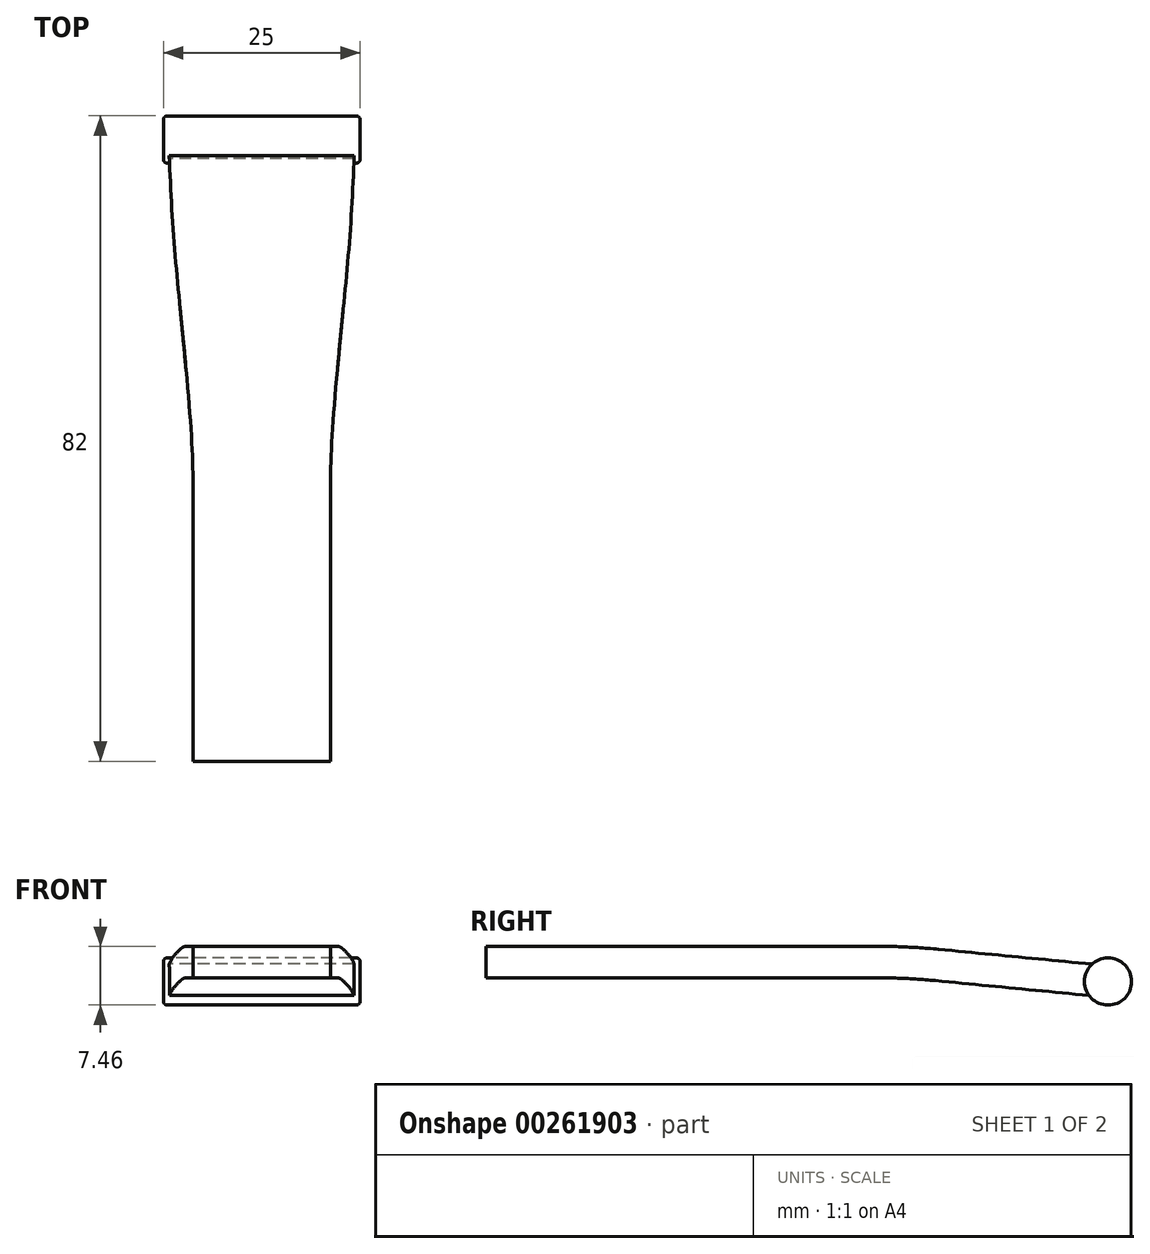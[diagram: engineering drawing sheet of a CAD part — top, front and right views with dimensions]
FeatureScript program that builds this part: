
annotation { "Feature Type Name" : "Feature", "Feature Type Description" : "" }
export const myFeature = defineFeature(function(context is Context, id is Id, definition is map)
    precondition{}
    {
        {
            var Q0;
            Q0=qCreatedBy(makeId("Right.planeOp"),FACE);
            var sketch = newSketch(context, id + "F0", { "sketchPlane" : qUnion([Q0])});
            skCircle(sketch, "E0", {"center": v(72.77, -2.11) * mm, "radius": 3 * mm});
            skLineSegment(sketch, "E1", {"start": v(-6.23, 2.35) * mm, "end": v(43.54, 2.35) * mm});
            skLineSegment(sketch, "E2", {"start": v(70.73, 0.1) * mm, "end": v(51.23, 1.98) * mm});
            skArc(sketch, "E3.filletArc", {"start": v(51.23, 1.98) * mm, "mid": v(47.4, 2.25) * mm, "end": v(43.54, 2.35) * mm});
            skLineSegment(sketch, "E4.0", {"start": v(-6.23, -1.65) * mm, "end": v(43.54, -1.65) * mm});
            skArc(sketch, "E4.1", {"start": v(50.85, -2) * mm, "mid": v(47.2, -1.74) * mm, "end": v(43.54, -1.65) * mm});
            skLineSegment(sketch, "E4.2", {"start": v(70.35, -3.9) * mm, "end": v(50.85, -2) * mm});
            skLineSegment(sketch, "E5", {"start": v(-6.23, 2.35) * mm, "end": v(-6.23, -1.65) * mm});
            skSolve(sketch);
        }
        {
            var Q0;
            Q0 = qSketchRegion(id + "F0", true);
            extrude(context, id + "F1", {"entities" : qUnion([Q0]), "endBound" : BoundingType.SYMMETRIC, "depth" : 23.5 * mm});
        }
        {
            var Q0;
            Q0=qCreatedBy(makeId("Top.planeOp"),FACE);
            var sketch = newSketch(context, id + "F2", { "sketchPlane" : qUnion([Q0])});
            skLineSegment(sketch, "E6", {"start": v(0, 80.88) * mm, "end": v(0, -19.14) * mm, "construction": true});
            skLineSegment(sketch, "E7.0", {"start": v(11.75, -6.23) * mm, "end": v(-11.75, -6.23) * mm, "construction": true});
            skLineSegment(sketch, "E8", {"start": v(0, -6.23) * mm, "end": v(8.75, -6.23) * mm});
            skLineSegment(sketch, "E9", {"start": v(8.75, -6.23) * mm, "end": v(8.75, 24.09) * mm});
            skLineSegment(sketch, "E10.0", {"start": v(11.75, 70.73) * mm, "end": v(-11.75, 70.73) * mm, "construction": true});
            skFitSpline(sketch, "E11", {"points": [v(11.75, 70.73) * mm, v(11.12, 59.65) * mm, v(8.94, 35.14) * mm, v(8.75, 24.09) * mm], "startDerivative": vector(-1.3, -33.28) * mm, "endDerivative": vector(0, -38.84) * mm});
            skLineSegment(sketch, "E12.MirrorCS", {"start": v(-8.75, -6.23) * mm, "end": v(-8.75, 24.09) * mm});
            skFitSpline(sketch, "E13.MirrorCS", {"points": [v(-11.75, 70.73) * mm, v(-11.12, 59.65) * mm, v(-8.94, 35.14) * mm, v(-8.75, 24.09) * mm], "startDerivative": vector(1.3, -33.28) * mm, "endDerivative": vector(0, -38.84) * mm});
            skLineSegment(sketch, "E14", {"start": v(-11.75, 70.73) * mm, "end": v(-11.75, -6.23) * mm});
            skLineSegment(sketch, "E15", {"start": v(-8.75, -6.23) * mm, "end": v(-11.75, -6.23) * mm});
            skLineSegment(sketch, "E16", {"start": v(8.75, -6.23) * mm, "end": v(11.75, -6.23) * mm});
            skLineSegment(sketch, "E17", {"start": v(11.75, 70.73) * mm, "end": v(11.75, -6.23) * mm});
            skSolve(sketch);
        }
        {
            var Q0;
            Q0 = qSketchRegion(id + "F2", true);
            extrude(context, id + "F3", {"entities" : qUnion([Q0]), "operationType" : NewBodyOperationType.REMOVE, "endBound" : BoundingType.SYMMETRIC, "oppositeDirection" : true, "depth" : 20.4 * mm});
        }
        {
            var Q0;
            Q0=qCreatedBy(makeId("Right.planeOp"),FACE);
            var sketch = newSketch(context, id + "F4", { "sketchPlane" : qUnion([Q0])});
            skCircle(sketch, "E18", {"center": v(72.77, -2.11) * mm, "radius": 3 * mm});
            skPoint(sketch, "E19.0.end.orphan", {"position": v(70.73, 0.1) * mm});
            skPoint(sketch, "E19.0.start.orphan", {"position": v(70.73, -4.32) * mm});
            skSolve(sketch);
        }
        {
            var Q0;
            Q0 = qSketchRegion(id + "F4", true);
            extrude(context, id + "F5", {"entities" : qUnion([Q0]), "operationType" : NewBodyOperationType.ADD, "endBound" : BoundingType.SYMMETRIC, "depth" : 25 * mm});
        }
        {
            var Q0;
            Q0=makeQuery(id+"F5.opExtrude","CAP_FACE",FACE,{"disambiguationData":[OSD([sQuery(id+"F4.wireOp",EDGE,"E18")])],"isStart":false});
            var Q1;
            Q1=makeQuery(id+"F5.opExtrude","CAP_FACE",FACE,{"disambiguationData":[OSD([sQuery(id+"F4.wireOp",EDGE,"E18")])],"isStart":true});
            fillet(context, id + "F6", {"entities" : qUnion([Q0, Q1]), "radius" : .5 * mm, "tangentPropagation" : true, "allowEdgeOverflow" : false});
        }
        {
            var Q0;
            Q0=qCreatedBy(makeId("Right.planeOp"),FACE);
            var sketch = newSketch(context, id + "F7", { "sketchPlane" : qUnion([Q0])});
            skSolve(sketch);
        }
        {
            var Q0;
            Q0=makeQuery(id+"F1.opExtrude","SWEPT_FACE",FACE,{"disambiguationData":[OSD([sQuery(id+"F0.wireOp",EDGE,"E5")])]});
            var sketch = newSketch(context, id + "F8", { "sketchPlane" : qUnion([Q0])});
            skLineSegment(sketch, "E20.1", {"start": v(8.75, -1.65) * mm, "end": v(8.75, 2.35) * mm});
            skLineSegment(sketch, "E20.2", {"start": v(8.75, 2.35) * mm, "end": v(-8.75, 2.35) * mm});
            skLineSegment(sketch, "E20.3", {"start": v(-8.75, -1.65) * mm, "end": v(-8.75, 2.35) * mm});
            skLineSegment(sketch, "E20.4", {"start": v(8.75, -1.65) * mm, "end": v(-8.75, -1.65) * mm});
            skPoint(sketch, "E20.5", {"position": v(-8.75, 0.35) * mm});
            skSolve(sketch);
        }
        {
            var Q0;
            Q0=makeQuery(id+"F8.imprint","IMPRINT",FACE,{"disambiguationData":[TD([[makeQuery(id+"F8.imprint","IMPRINT",EDGE,{"derivedFrom":sQuery(id+"F8.wireOp",EDGE,"E20.1")}),1.0]])]});
            cPlane(context, id + "F9", {"entities" : qUnion([Q0]), "cplaneType" : CPlaneType.OFFSET, "offset" : 32 * mm, "width" : 150 * mm, "height" : 150 * mm});
        }
        {
            var Q0;
            Q0=qCreatedBy(id+"F9.planeOp",FACE);
            var sketch = newSketch(context, id + "F10", { "sketchPlane" : qUnion([Q0])});
            skLineSegment(sketch, "E21", {"start": v(-10, 2.35) * mm, "end": v(10, 2.35) * mm});
            skLineSegment(sketch, "E22", {"start": v(9, -2.04) * mm, "end": v(-9, -2.04) * mm});
            skLineSegment(sketch, "E23", {"start": v(0, 0) * mm, "end": v(0, 1.9) * mm, "construction": true});
            skArc(sketch, "E24", {"start": v(-10, 2.35) * mm, "mid": v(-9.66, 0.12) * mm, "end": v(-9, -2.04) * mm});
            skArc(sketch, "E25.MirrorCS", {"start": v(10, 2.35) * mm, "mid": v(9.66, 0.12) * mm, "end": v(9, -2.04) * mm});
            skSolve(sketch);
        }
        {
            var Q0;
            Q0=qCreatedBy(id+"F9.planeOp",FACE);
            cPlane(context, id + "F11", {"entities" : qUnion([Q0]), "cplaneType" : CPlaneType.OFFSET, "offset" : 15 * mm, "width" : 150 * mm, "height" : 150 * mm});
        }
        {
            var Q0;
            Q0=qCreatedBy(id+"F11.planeOp",FACE);
            var sketch = newSketch(context, id + "F12", { "sketchPlane" : qUnion([Q0])});
            skLineSegment(sketch, "E26", {"start": v(0, 8.95) * mm, "end": v(0, -8.78) * mm, "construction": true});
            skLineSegment(sketch, "E27.0", {"start": v(-12.5, 8.95) * mm, "end": v(-12.5, -8.78) * mm, "construction": true});
            skLineSegment(sketch, "E28.0", {"start": v(12.5, 8.95) * mm, "end": v(12.5, -8.78) * mm, "construction": true});
            skLineSegment(sketch, "E29.0", {"start": v(20, 2.35) * mm, "end": v(-10, 2.35) * mm, "construction": true});
            skLineSegment(sketch, "E30", {"start": v(-10, 2.35) * mm, "end": v(-15.15, 2.35) * mm, "construction": true});
            skArc(sketch, "E31", {"start": v(-12.5, 2.35) * mm, "mid": v(0, 0.75) * mm, "end": v(12.5, 2.35) * mm});
            skLineSegment(sketch, "E32.0", {"start": v(-10, -5.15) * mm, "end": v(-15.15, -5.15) * mm, "construction": true});
            skLineSegment(sketch, "E32.1", {"start": v(20, -5.15) * mm, "end": v(-10, -5.15) * mm, "construction": true});
            skArc(sketch, "E33", {"start": v(-12.5, 2.35) * mm, "mid": v(-11.2, -0.29) * mm, "end": v(-9.26, -2.48) * mm});
            skArc(sketch, "E34.MirrorCS", {"start": v(12.5, 2.35) * mm, "mid": v(11.2, -0.29) * mm, "end": v(9.26, -2.48) * mm});
            skArc(sketch, "E35", {"start": v(-9.26, -2.48) * mm, "mid": v(0, -5.1) * mm, "end": v(9.26, -2.48) * mm});
            skSolve(sketch);
        }
        {
            var Q0;
            Q0=qCreatedBy(id+"F11.planeOp",FACE);
            cPlane(context, id + "F13", {"entities" : qUnion([Q0]), "cplaneType" : CPlaneType.OFFSET, "offset" : 15 * mm, "width" : 150 * mm, "height" : 150 * mm});
        }
        {
            var Q0;
            Q0=qCreatedBy(id+"F13.planeOp",FACE);
            var sketch = newSketch(context, id + "F14", { "sketchPlane" : qUnion([Q0])});
            skLineSegment(sketch, "E36.0", {"start": v(28.72, 2.35) * mm, "end": v(-25.72, 2.35) * mm, "construction": true});
            skLineSegment(sketch, "E37.0", {"start": v(0, 8.95) * mm, "end": v(0, -8.78) * mm, "construction": true});
            skLineSegment(sketch, "E38.0", {"start": v(-22, 8.95) * mm, "end": v(-22, -8.78) * mm, "construction": true});
            skLineSegment(sketch, "E39.0", {"start": v(22, 8.95) * mm, "end": v(22, -8.78) * mm, "construction": true});
            skLineSegment(sketch, "E40.0", {"start": v(28.72, -10.15) * mm, "end": v(-25.72, -10.15) * mm, "construction": true});
            skArc(sketch, "E41", {"start": v(-22, 2.35) * mm, "mid": v(-18.65, -2.55) * mm, "end": v(-14.42, -6.7) * mm});
            skArc(sketch, "E42.MirrorCS", {"start": v(22, 2.35) * mm, "mid": v(18.65, -2.55) * mm, "end": v(14.42, -6.7) * mm});
            skArc(sketch, "E43", {"start": v(-14.42, -6.7) * mm, "mid": v(0, -9.59) * mm, "end": v(14.42, -6.7) * mm});
            skArc(sketch, "E44", {"start": v(-22, 2.35) * mm, "mid": v(0, -4.15) * mm, "end": v(22, 2.35) * mm});
            skSolve(sketch);
        }
        {
            var Q0;
            Q0=qCreatedBy(id+"F13.planeOp",FACE);
            cPlane(context, id + "F15", {"entities" : qUnion([Q0]), "cplaneType" : CPlaneType.OFFSET, "offset" : 9 * mm, "width" : 150 * mm, "height" : 150 * mm});
        }
        {
            var Q0;
            Q0=qCreatedBy(id+"F15.planeOp",FACE);
            var sketch = newSketch(context, id + "F16", { "sketchPlane" : qUnion([Q0])});
            skLineSegment(sketch, "E45.0", {"start": v(0, 8.95) * mm, "end": v(0, -8.78) * mm, "construction": true});
            skLineSegment(sketch, "E46.0", {"start": v(28.72, 2.35) * mm, "end": v(-28.62, 2.35) * mm, "construction": true});
            skLineSegment(sketch, "E47.0", {"start": v(-27.5, 8.95) * mm, "end": v(-27.5, -8.78) * mm, "construction": true});
            skLineSegment(sketch, "E48.0", {"start": v(27.5, 8.95) * mm, "end": v(27.5, -8.78) * mm, "construction": true});
            skLineSegment(sketch, "E49.0", {"start": v(28.72, -12.9) * mm, "end": v(-25.72, -12.9) * mm, "construction": true});
            skArc(sketch, "E50", {"start": v(-27.5, 2.35) * mm, "mid": v(0, -7.55) * mm, "end": v(27.5, 2.35) * mm});
            skArc(sketch, "E51", {"start": v(16.59, -8.25) * mm, "mid": v(22.67, -3.6) * mm, "end": v(27.5, 2.35) * mm});
            skArc(sketch, "E52.MirrorCS", {"start": v(-16.59, -8.25) * mm, "mid": v(-22.67, -3.6) * mm, "end": v(-27.5, 2.35) * mm});
            skArc(sketch, "E53", {"start": v(-16.59, -8.25) * mm, "mid": v(0, -12.73) * mm, "end": v(16.59, -8.25) * mm});
            skSolve(sketch);
        }
        {
            var Q0;
            Q0=qCreatedBy(id+"F15.planeOp",FACE);
            cPlane(context, id + "F17", {"entities" : qUnion([Q0]), "cplaneType" : CPlaneType.OFFSET, "offset" : 25 * mm, "width" : 150 * mm, "height" : 150 * mm});
        }
        {
            var Q0;
            Q0=qCreatedBy(id+"F17.planeOp",FACE);
            var sketch = newSketch(context, id + "F18", { "sketchPlane" : qUnion([Q0])});
            skLineSegment(sketch, "E54.0", {"start": v(0, 8.95) * mm, "end": v(0, -8.78) * mm, "construction": true});
            skLineSegment(sketch, "E55.0", {"start": v(28.72, 2.35) * mm, "end": v(-28.62, 2.35) * mm, "construction": true});
            skLineSegment(sketch, "E56.0", {"start": v(-26.75, 8.95) * mm, "end": v(-26.75, -8.78) * mm, "construction": true});
            skLineSegment(sketch, "E57.MirrorCS", {"start": v(26.75, 8.95) * mm, "end": v(26.75, -8.78) * mm, "construction": true});
            skLineSegment(sketch, "E58.0", {"start": v(28.72, -14.45) * mm, "end": v(-28.62, -14.45) * mm, "construction": true});
            skArc(sketch, "E59", {"start": v(-26.75, 2.35) * mm, "mid": v(0, -10.33) * mm, "end": v(26.75, 2.35) * mm});
            skArc(sketch, "E60", {"start": v(17.45, -8.66) * mm, "mid": v(22.78, -3.73) * mm, "end": v(26.75, 2.35) * mm});
            skArc(sketch, "E61.MirrorCS", {"start": v(-17.45, -8.66) * mm, "mid": v(-22.78, -3.73) * mm, "end": v(-26.75, 2.35) * mm});
            skArc(sketch, "E62", {"start": v(-17.45, -8.66) * mm, "mid": v(0, -14.06) * mm, "end": v(17.45, -8.66) * mm});
            skSolve(sketch);
        }
        {
            var Q0;
            Q0=qCreatedBy(id+"F17.planeOp",FACE);
            cPlane(context, id + "F19", {"entities" : qUnion([Q0]), "cplaneType" : CPlaneType.OFFSET, "offset" : 25 * mm, "width" : 150 * mm, "height" : 150 * mm});
        }
        {
            var Q0;
            Q0=qCreatedBy(id+"F19.planeOp",FACE);
            var sketch = newSketch(context, id + "F20", { "sketchPlane" : qUnion([Q0])});
            skLineSegment(sketch, "E63.0", {"start": v(28.72, 2.35) * mm, "end": v(-28.62, 2.35) * mm, "construction": true});
            skLineSegment(sketch, "E64.0", {"start": v(0, 8.95) * mm, "end": v(0, -8.78) * mm, "construction": true});
            skLineSegment(sketch, "E65.0", {"start": v(-23.12, 8.95) * mm, "end": v(-23.12, -8.78) * mm, "construction": true});
            skLineSegment(sketch, "E66.MirrorCS", {"start": v(23.12, 8.95) * mm, "end": v(23.12, -8.78) * mm, "construction": true});
            skLineSegment(sketch, "E67.0", {"start": v(28.72, -8.4) * mm, "end": v(-28.62, -8.4) * mm, "construction": true});
            skArc(sketch, "E68", {"start": v(-23.13, 2.35) * mm, "mid": v(-19.17, -2.15) * mm, "end": v(-14.35, -5.72) * mm});
            skArc(sketch, "E69.MirrorCS", {"start": v(23.13, 2.35) * mm, "mid": v(19.17, -2.15) * mm, "end": v(14.35, -5.72) * mm});
            skArc(sketch, "E70", {"start": v(-14.35, -5.72) * mm, "mid": v(0, -8.28) * mm, "end": v(14.35, -5.72) * mm});
            skArc(sketch, "E71", {"start": v(-23.13, 2.35) * mm, "mid": v(0, -5.15) * mm, "end": v(23.13, 2.35) * mm});
            skSolve(sketch);
        }
        {
            var Q0;
            Q0=qCreatedBy(id+"F19.planeOp",FACE);
            cPlane(context, id + "F21", {"entities" : qUnion([Q0]), "cplaneType" : CPlaneType.OFFSET, "offset" : 18 * mm, "width" : 150 * mm, "height" : 150 * mm});
        }
        {
            var Q0;
            Q0=qCreatedBy(id+"F21.planeOp",FACE);
            var sketch = newSketch(context, id + "F22", { "sketchPlane" : qUnion([Q0])});
            skLineSegment(sketch, "E72.0", {"start": v(0, 8.95) * mm, "end": v(0, -8.78) * mm, "construction": true});
            skLineSegment(sketch, "E73.0", {"start": v(28.72, 2.35) * mm, "end": v(-28.62, 2.35) * mm, "construction": true});
            skLineSegment(sketch, "E74.0", {"start": v(-17.88, 8.95) * mm, "end": v(-17.88, -8.78) * mm, "construction": true});
            skLineSegment(sketch, "E75.MirrorCS", {"start": v(17.88, 8.95) * mm, "end": v(17.88, -8.78) * mm, "construction": true});
            skLineSegment(sketch, "E76.0", {"start": v(28.72, -1.65) * mm, "end": v(-28.62, -1.65) * mm, "construction": true});
            skArc(sketch, "E77", {"start": v(-17.88, 2.35) * mm, "mid": v(0, 0.74) * mm, "end": v(17.88, 2.35) * mm});
            skArc(sketch, "E78", {"start": v(-17.88, 2.35) * mm, "mid": v(-14.45, 0.6) * mm, "end": v(-10.85, -0.77) * mm});
            skArc(sketch, "E79.MirrorCS", {"start": v(17.88, 2.35) * mm, "mid": v(14.45, 0.6) * mm, "end": v(10.85, -0.77) * mm});
            skArc(sketch, "E80", {"start": v(-10.85, -0.77) * mm, "mid": v(0, -1.6) * mm, "end": v(10.85, -0.77) * mm});
            skSolve(sketch);
        }
        {
            var Q0;
            Q0=qCreatedBy(id+"F21.planeOp",FACE);
            cPlane(context, id + "F23", {"entities" : qUnion([Q0]), "cplaneType" : CPlaneType.OFFSET, "offset" : 8.7 * mm, "width" : 150 * mm, "height" : 150 * mm});
        }
    });
